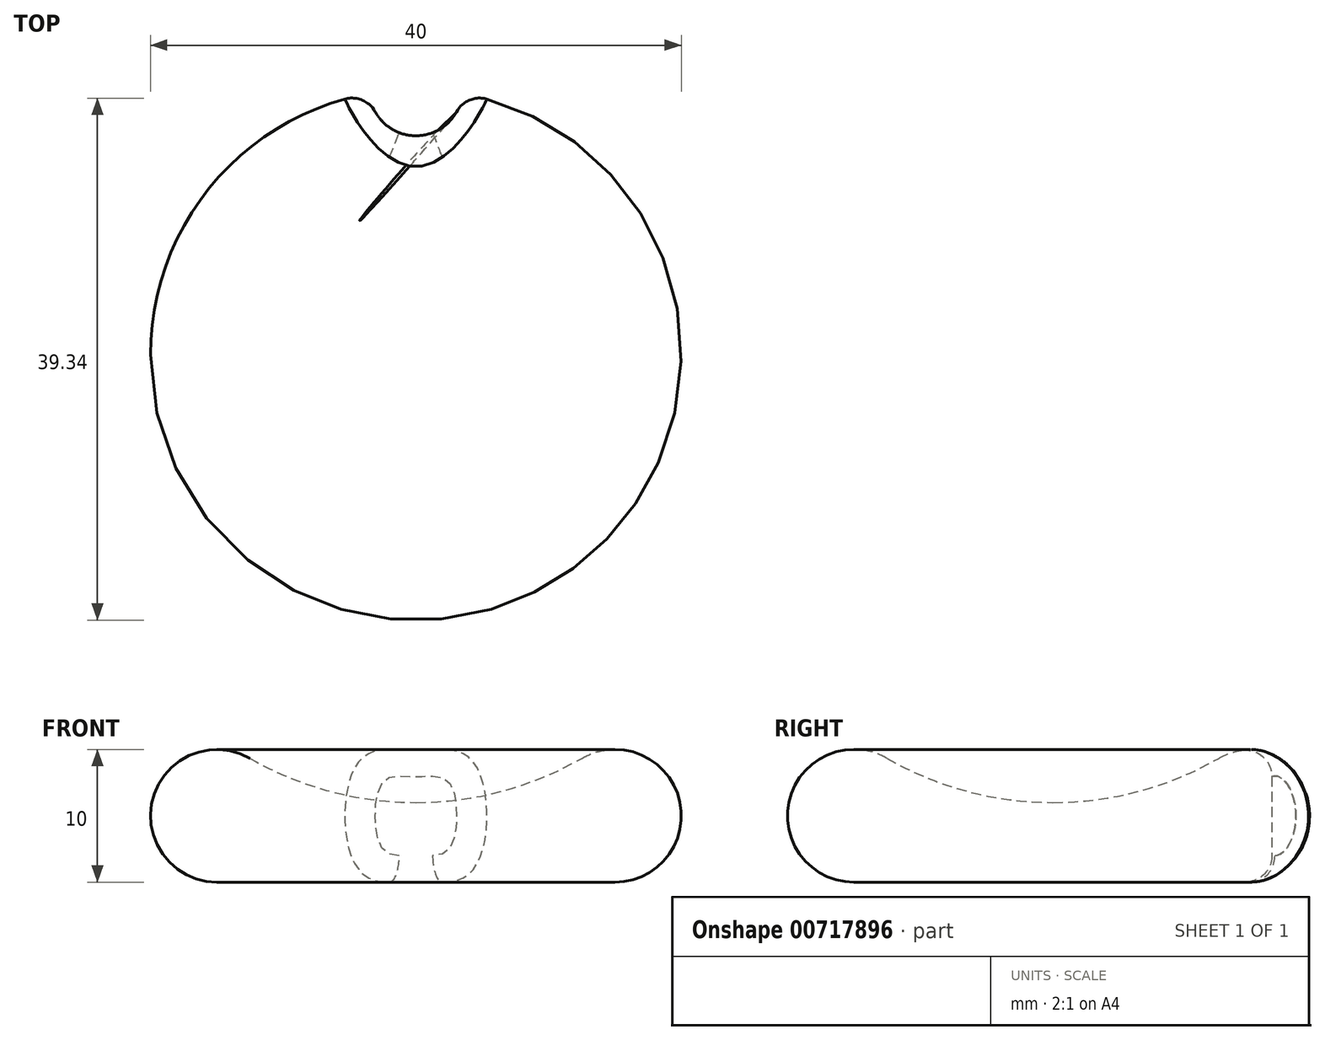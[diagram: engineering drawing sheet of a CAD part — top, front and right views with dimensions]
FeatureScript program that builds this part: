
annotation { "Feature Type Name" : "Feature", "Feature Type Description" : "" }
export const myFeature = defineFeature(function(context is Context, id is Id, definition is map)
    precondition{}
    {
        {
            var Q0;
            Q0=qCreatedBy(makeId("Front.planeOp"),FACE);
            var sketch = newSketch(context, id + "F0", { "sketchPlane" : qUnion([Q0])});
            skArc(sketch, "E0", {"start": v(-12.51, 9.34) * mm, "mid": v(-6.47, 6.85) * mm, "end": v(0, 6) * mm});
            skArc(sketch, "E1", {"start": v(-12.51, 9.34) * mm, "mid": v(-19.83, 6.29) * mm, "end": v(-15, 0) * mm});
            skLineSegment(sketch, "E2", {"start": v(-15, 0) * mm, "end": v(0, 0) * mm});
            skLineSegment(sketch, "E3", {"start": v(0, 0) * mm, "end": v(0, 6) * mm});
            skSolve(sketch);
        }
        {
            var Q0;
            Q0=makeQuery(id+"F0.imprint","IMPRINT",FACE,{"disambiguationData":[TD([[makeQuery(id+"F0.imprint","IMPRINT",EDGE,{"derivedFrom":sQuery(id+"F0.wireOp",EDGE,"E0")}),-1.0]])]});
            var Q1;
            Q1=sQuery(id+"F0.wireOp",EDGE,"E3");
            revolve(context, id + "F1", {"surfaceOperationType" : NewSurfaceOperationType.NEW, "entities" : qUnion([Q0]), "axis" : qUnion([Q1]), "revolveType" : RevolveType.FULL});
        }
        {
            var Q0;
            Q0=qCreatedBy(makeId("Top.planeOp"),FACE);
            var sketch = newSketch(context, id + "F2", { "sketchPlane" : qUnion([Q0])});
            skCircle(sketch, "E4", {"center": v(0, 20) * mm, "radius": 3.5 * mm});
            skSolve(sketch);
        }
        {
            var Q0;
            Q0=makeQuery(id+"F2.imprint","IMPRINT",FACE,{"disambiguationData":[TD([[makeQuery(id+"F2.imprint","IMPRINT",EDGE,{"derivedFrom":sQuery(id+"F2.wireOp",EDGE,"E4")}),1.0]])]});
            extrude(context, id + "F3", {"entities" : qUnion([Q0]), "operationType" : NewBodyOperationType.REMOVE, "oppositeDirection" : true, "depth" : -10 * mm, "offsetDistance" : 25 * mm});
        }
        {
            var Q0;
            Q0=makeQuery(id+"F3.boolean.opBoolean","INTERSECT",EDGE,{"derivedFrom":[makeQuery(id+"F1.opRevolve","SWEPT_FACE",FACE,{"disambiguationData":[OSD([sQuery(id+"F0.wireOp",EDGE,"E1")])]}),makeQuery(id+"F3.opExtrude","SWEPT_FACE",FACE,{"disambiguationData":[OSD([sQuery(id+"F2.wireOp",EDGE,"E4")])]})]});
            var Q1;
            Q1=makeQuery(id+"F3.boolean.opBoolean","COPY",FACE,{"derivedFrom":makeQuery(id+"F3.opExtrude","SWEPT_FACE",FACE,{"disambiguationData":[OSD([sQuery(id+"F2.wireOp",EDGE,"E4")])]})});
            fillet(context, id + "F4", {"entities" : qUnion([Q0, Q1]), "radius" : 2 * mm, "tangentPropagation" : true, "allowEdgeOverflow" : false});
        }
    });
